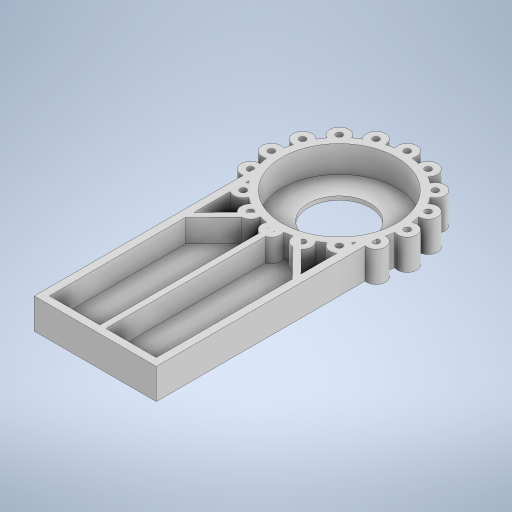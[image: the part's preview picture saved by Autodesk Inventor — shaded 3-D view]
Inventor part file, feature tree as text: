
AUTODESK INVENTOR PART (.ipt)
format: ipt  version: 2024 (Build 280153000, 153)  size: 406,016 bytes
history: native  units: mm
features: extrude x5, sketch x4, projected_geometry x1
ambient origin geometry x8: Origin, YZ Plane, XZ Plane, XY Plane, X Axis, Y Axis, Z Axis, Center Point
bodies: Solid1 (feature_tree)
feature tree (10):
  extrude  "Extrusion1"  Depth=160.0mm
  extrude  "Extrusion2"  Depth=150.0mm
  extrude  "Extrusion3"  Depth=5.0mm TaperAngle=0.0deg
  extrude  "Extrusion4"  Depth=10.0mm
  extrude  "Extrusion5"  Depth=8.0mm
  sketch  "Sketch1"  dims[d0=160.0mm d1=400.0mm]
  sketch  "Sketch3"  dims[d2=80.0mm d3=150.0mm]
  projected_geometry  "Projected Loop1"
  sketch  "Sketch4"  dims[d4=40.0mm d5=0.0mm d6=5.0mm d7=0.0mm]
  sketch  "Sketch5"  dims[d8=10.0mm d9=10.0mm d10=8.0mm d11=8.0mm d12=30.0mm d13=0.0mm d14=81.0mm d15=40.0mm d16=0.0mm d17=8.1mm d18=160.0mm d20=360.0deg d22=10.0mm d23=0.0mm]
